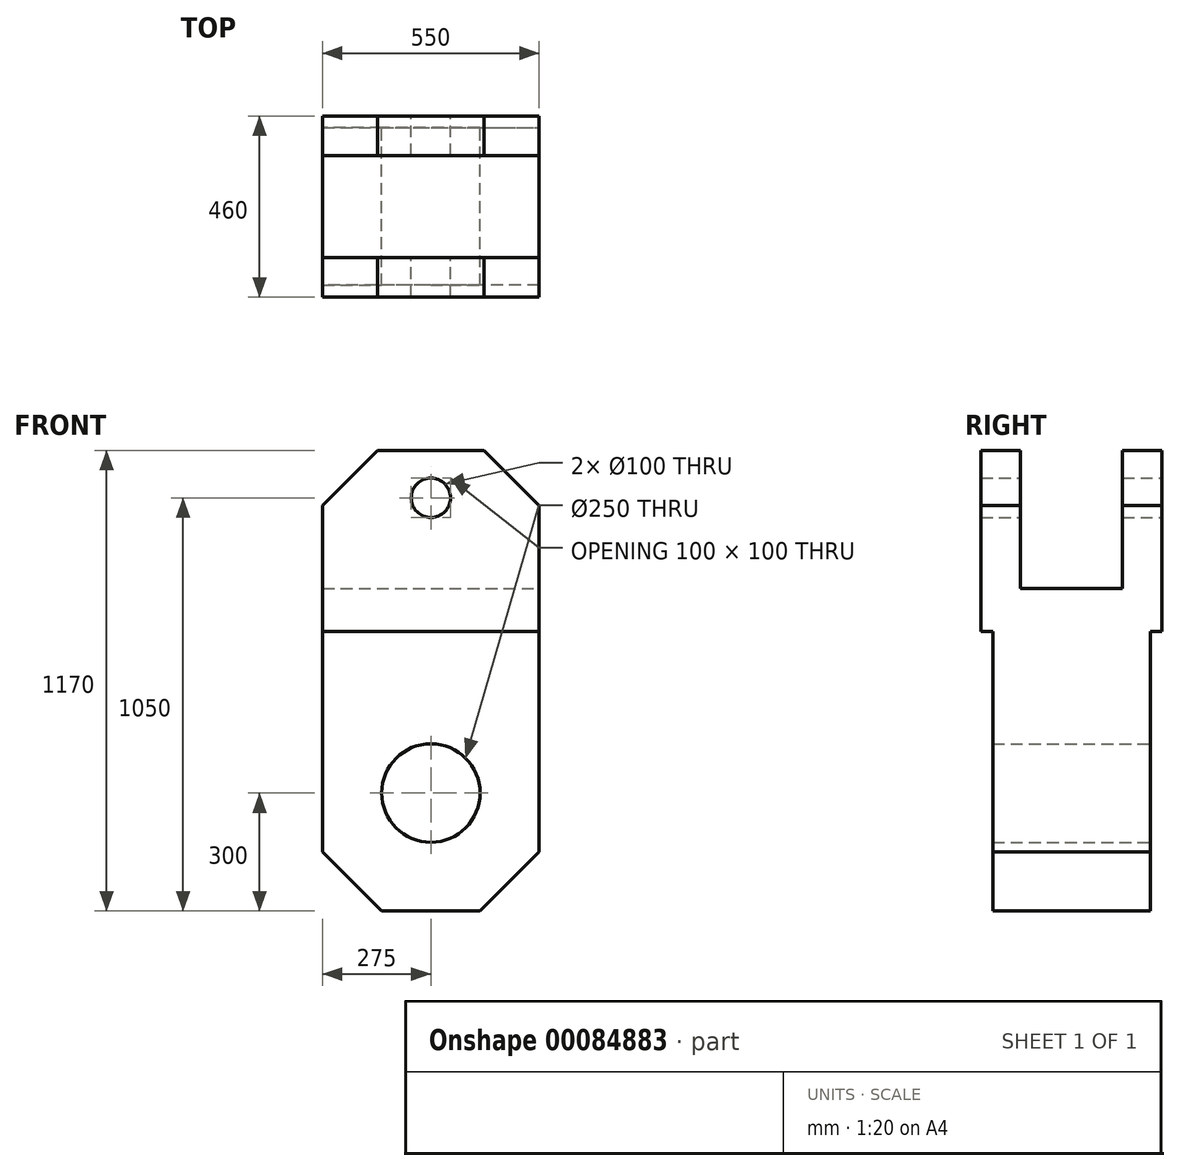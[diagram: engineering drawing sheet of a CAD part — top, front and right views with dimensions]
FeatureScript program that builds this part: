
annotation { "Feature Type Name" : "Feature", "Feature Type Description" : "" }
export const myFeature = defineFeature(function(context is Context, id is Id, definition is map)
    precondition{}
    {
        {
            var Q0;
            Q0=qCreatedBy(makeId("Front.planeOp"),FACE);
            var sketch = newSketch(context, id + "F0", { "sketchPlane" : qUnion([Q0])});
            skLineSegment(sketch, "E0.top", {"start": v(-135, 120) * mm, "end": v(135, 120) * mm});
            skLineSegment(sketch, "E0.left", {"start": v(-275, -120) * mm, "end": v(-275, -20) * mm});
            skLineSegment(sketch, "E0.right", {"start": v(275, -120) * mm, "end": v(275, -20) * mm});
            skPoint(sketch, "E0.middle", {"position": v(0, 0) * mm});
            skLineSegment(sketch, "E1", {"start": v(-275, -20) * mm, "end": v(-135, 120) * mm});
            skLineSegment(sketch, "E2", {"start": v(275, -20) * mm, "end": v(135, 120) * mm});
            skLineSegment(sketch, "E3.top", {"start": v(-125, -1050) * mm, "end": v(125, -1050) * mm});
            skLineSegment(sketch, "E3.left", {"start": v(-275, -120) * mm, "end": v(-275, -900) * mm});
            skLineSegment(sketch, "E3.right", {"start": v(275, -120) * mm, "end": v(275, -900) * mm});
            skLineSegment(sketch, "E4", {"start": v(-275, -900) * mm, "end": v(-125, -1050) * mm});
            skLineSegment(sketch, "E5", {"start": v(275, -900) * mm, "end": v(125, -1050) * mm});
            skCircle(sketch, "E6", {"center": v(0, 0) * mm, "radius": 50 * mm});
            skCircle(sketch, "E7", {"center": v(0, -750) * mm, "radius": 125 * mm});
            skPoint(sketch, "E8.orphan", {"position": v(-275, 120) * mm});
            skPoint(sketch, "E9.orphan", {"position": v(275, 120) * mm});
            skPoint(sketch, "E10.orphan", {"position": v(275, -1050) * mm});
            skPoint(sketch, "E11.orphan", {"position": v(-275, -1050) * mm});
            skSolve(sketch);
        }
        {
            var Q0;
            Q0=makeQuery(id+"F0.imprint","IMPRINT",FACE,{"disambiguationData":[TD([[makeQuery(id+"F0.imprint","IMPRINT",EDGE,{"derivedFrom":sQuery(id+"F0.wireOp",EDGE,"E0.top")}),-1.0]])]});
            extrude(context, id + "F1", {"entities" : qUnion([Q0]), "depth" : 460 * mm});
        }
        {
            var Q0;
            Q0=makeQuery(id+"F1.opExtrude","SWEPT_FACE",FACE,{"disambiguationData":[OSD([sQuery(id+"F0.wireOp",EDGE,"E0.right"),sQuery(id+"F0.wireOp",EDGE,"E3.right")])]});
            var sketch = newSketch(context, id + "F2", { "sketchPlane" : qUnion([Q0])});
            skLineSegment(sketch, "E12.bottom", {"start": v(-360, -230) * mm, "end": v(-100, -230) * mm});
            skLineSegment(sketch, "E12.top", {"start": v(-360, 190) * mm, "end": v(-100, 190) * mm});
            skLineSegment(sketch, "E12.left", {"start": v(-360, -230) * mm, "end": v(-360, 190) * mm});
            skLineSegment(sketch, "E12.right", {"start": v(-100, -230) * mm, "end": v(-100, 190) * mm});
            skPoint(sketch, "E12.middle", {"position": v(-230, -20) * mm});
            skSolve(sketch);
        }
        {
            var Q0;
            Q0 = qSketchRegion(id + "F2", true);
            extrude(context, id + "F3", {"entities" : qUnion([Q0]), "operationType" : NewBodyOperationType.REMOVE, "endBound" : BoundingType.THROUGH_ALL, "oppositeDirection" : true, "depth" : 25 * mm});
        }
        {
            var Q0;
            Q0=makeQuery(id+"F1.opExtrude","CAP_FACE",FACE,{"disambiguationData":[OSD([sQuery(id+"F0.wireOp",EDGE,"E0.top"),sQuery(id+"F0.wireOp",EDGE,"E0.left"),sQuery(id+"F0.wireOp",EDGE,"E0.right"),sQuery(id+"F0.wireOp",EDGE,"E1"),sQuery(id+"F0.wireOp",EDGE,"E2"),sQuery(id+"F0.wireOp",EDGE,"E3.top"),sQuery(id+"F0.wireOp",EDGE,"E3.left"),sQuery(id+"F0.wireOp",EDGE,"E3.right"),sQuery(id+"F0.wireOp",EDGE,"E4"),sQuery(id+"F0.wireOp",EDGE,"E5"),sQuery(id+"F0.wireOp",EDGE,"E6"),sQuery(id+"F0.wireOp",EDGE,"E7")])],"isStart":true});
            var sketch = newSketch(context, id + "F4", { "sketchPlane" : qUnion([Q0])});
            skLineSegment(sketch, "E13.bottom", {"start": v(275, -1050) * mm, "end": v(-275, -1050) * mm});
            skLineSegment(sketch, "E13.top", {"start": v(275, -340) * mm, "end": v(-275, -340) * mm});
            skLineSegment(sketch, "E13.left", {"start": v(275, -1050) * mm, "end": v(275, -340) * mm});
            skLineSegment(sketch, "E13.right", {"start": v(-275, -1050) * mm, "end": v(-275, -340) * mm});
            skSolve(sketch);
        }
        {
            var Q0;
            Q0 = qSketchRegion(id + "F4", true);
            extrude(context, id + "F5", {"entities" : qUnion([Q0]), "operationType" : NewBodyOperationType.REMOVE, "oppositeDirection" : true, "depth" : 30 * mm});
        }
        {
            var Q0;
            Q0=makeQuery(id+"F1.opExtrude","CAP_FACE",FACE,{"disambiguationData":[OSD([sQuery(id+"F0.wireOp",EDGE,"E0.top"),sQuery(id+"F0.wireOp",EDGE,"E0.left"),sQuery(id+"F0.wireOp",EDGE,"E0.right"),sQuery(id+"F0.wireOp",EDGE,"E1"),sQuery(id+"F0.wireOp",EDGE,"E2"),sQuery(id+"F0.wireOp",EDGE,"E3.top"),sQuery(id+"F0.wireOp",EDGE,"E3.left"),sQuery(id+"F0.wireOp",EDGE,"E3.right"),sQuery(id+"F0.wireOp",EDGE,"E4"),sQuery(id+"F0.wireOp",EDGE,"E5"),sQuery(id+"F0.wireOp",EDGE,"E6"),sQuery(id+"F0.wireOp",EDGE,"E7")])],"isStart":false});
            var sketch = newSketch(context, id + "F6", { "sketchPlane" : qUnion([Q0])});
            skLineSegment(sketch, "E14.bottom", {"start": v(275, -1050) * mm, "end": v(-275, -1050) * mm});
            skLineSegment(sketch, "E14.top", {"start": v(275, -340) * mm, "end": v(-275, -340) * mm});
            skLineSegment(sketch, "E14.left", {"start": v(275, -1050) * mm, "end": v(275, -340) * mm});
            skLineSegment(sketch, "E14.right", {"start": v(-275, -1050) * mm, "end": v(-275, -340) * mm});
            skSolve(sketch);
        }
        {
            var Q0;
            Q0 = qSketchRegion(id + "F6", true);
            extrude(context, id + "F7", {"entities" : qUnion([Q0]), "operationType" : NewBodyOperationType.REMOVE, "oppositeDirection" : true, "depth" : 30 * mm});
        }
    });
